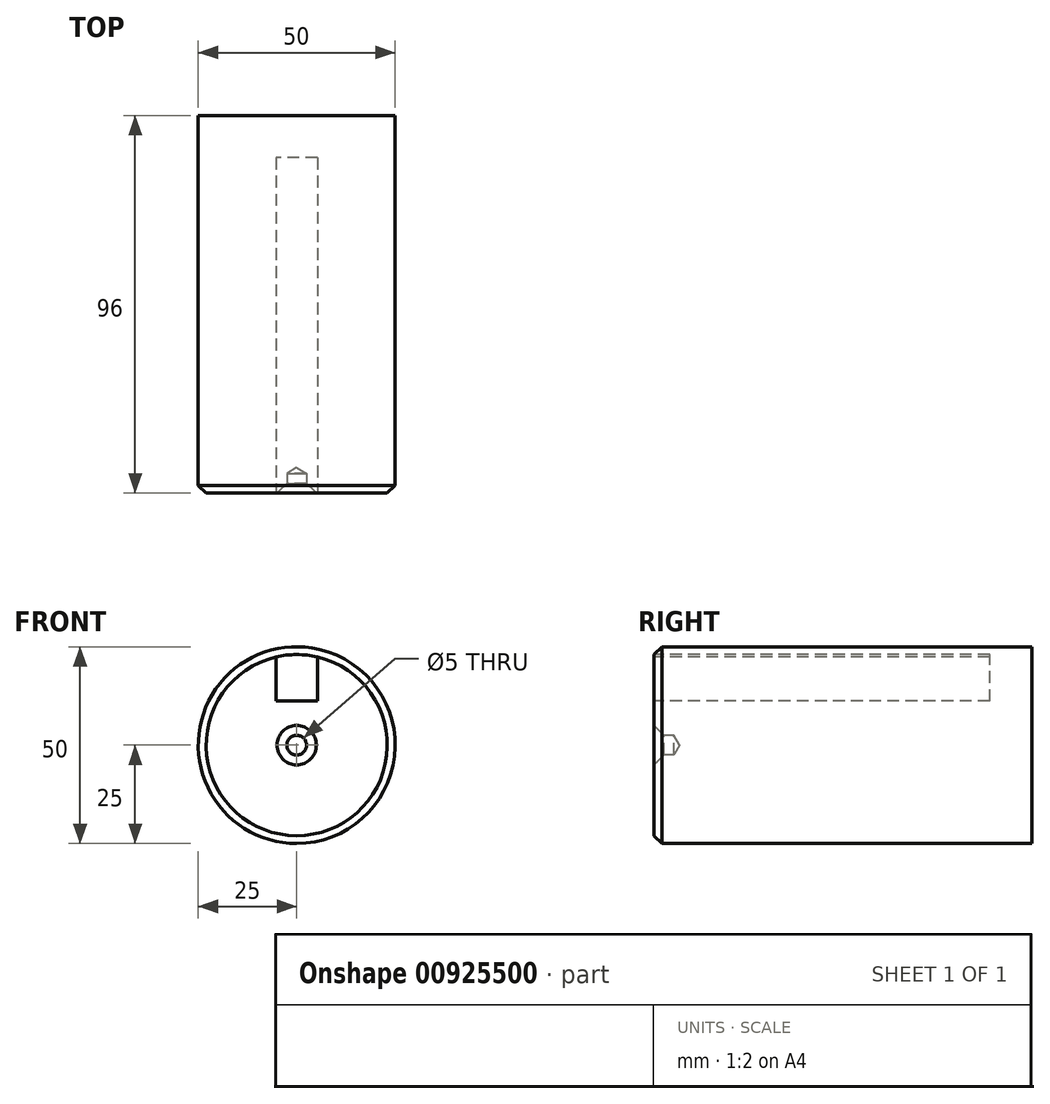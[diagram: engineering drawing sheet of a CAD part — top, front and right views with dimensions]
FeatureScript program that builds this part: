
annotation { "Feature Type Name" : "Feature", "Feature Type Description" : "" }
export const myFeature = defineFeature(function(context is Context, id is Id, definition is map)
    precondition{}
    {
        {
            var Q0;
            Q0=qCreatedBy(makeId("Front.planeOp"),FACE);
            var sketch = newSketch(context, id + "F0", { "sketchPlane" : qUnion([Q0])});
            skCircle(sketch, "E0", {"center": v(0, 0) * mm, "radius": 25 * mm});
            skSolve(sketch);
        }
        {
            var Q0;
            Q0=makeQuery(id+"F0.imprint","IMPRINT",FACE,{"disambiguationData":[TD([[makeQuery(id+"F0.imprint","IMPRINT",EDGE,{"derivedFrom":sQuery(id+"F0.wireOp",EDGE,"E0")}),1.0]])]});
            extrude(context, id + "F1", {"entities" : qUnion([Q0]), "depth" : 0 * mm, "offsetDistance" : 25 * mm, "hasSecondDirection" : true, "secondDirectionOppositeDirection" : true, "secondDirectionDepth" : 96 * mm});
        }
        {
            var Q0;
            Q0=makeQuery(id+"F1.opExtrude","CAP_EDGE",EDGE,{"disambiguationData":[OSD([sQuery(id+"F0.wireOp",EDGE,"E0")])],"isStart":false});
            chamfer(context, id + "F2", {"entities" : qUnion([Q0]), "chamferType" : ChamferType.OFFSET_ANGLE, "width" : 2 * mm, "oppositeDirection" : false, "angle" : 45 * degree, "tangentPropagation" : true});
        }
        {
            var Q0;
            Q0=makeQuery(id+"F1.opExtrude","CAP_FACE",FACE,{"disambiguationData":[OSD([sQuery(id+"F0.wireOp",EDGE,"E0")])],"isStart":false});
            var sketch = newSketch(context, id + "F3", { "sketchPlane" : qUnion([Q0])});
            skLineSegment(sketch, "E1", {"start": v(-5.25, 11.18) * mm, "end": v(4.75, 11.18) * mm});
            skLineSegment(sketch, "E2.MirrorCS", {"start": v(5.25, 11.18) * mm, "end": v(-4.75, 11.18) * mm});
            skLineSegment(sketch, "E3", {"start": v(5.25, 11.18) * mm, "end": v(5.25, 24.62) * mm});
            skLineSegment(sketch, "E4", {"start": v(-5.25, 11.18) * mm, "end": v(-5.25, 24.62) * mm});
            skArc(sketch, "E5", {"start": v(5.25, 24.62) * mm, "mid": v(0, 25.17) * mm, "end": v(-5.25, 24.62) * mm});
            skSolve(sketch);
        }
        {
            var Q0;
            {var subQ0=sQuery(id+"F3.wireOp",EDGE,"7XGwcHun-qUsb-BtbT-Hs0O-WZy7tM4iTs5j");Q0=makeQuery(id+"F3.imprint","IMPRINT",FACE,{"disambiguationData":[TD([[makeQuery(id+"F3.imprint","IMPRINT",EDGE,{"derivedFrom":subQ0}),1.0]])]});}
            var Q1;
            {var subQ6=sQuery(id+"F3.wireOp",EDGE,"E1");Q1=makeQuery(id+"F3.imprint","IMPRINT",FACE,{"disambiguationData":[TD([[makeQuery(id+"F3.imprint","IMPRINT",EDGE,{"derivedFrom":subQ6}),1.0]])]});}
            extrude(context, id + "F4", {"entities" : qUnion([Q0, Q1]), "operationType" : NewBodyOperationType.REMOVE, "oppositeDirection" : true, "depth" : 85.25 * mm, "offsetDistance" : 25 * mm});
        }
        {
            var Q0;
            Q0=qCreatedBy(makeId("Front.planeOp"),FACE);
            var sketch = newSketch(context, id + "F5", { "sketchPlane" : qUnion([Q0])});
            skPoint(sketch, "E6", {"position": v(0, 0) * mm});
            skSolve(sketch);
        }
        {
            var Q0;
            Q0=sQuery(id+"F5.wireOp",VERTEX,"E6");
            var Q1;
            Q1=makeQuery(id+"F1.opExtrude","SWEPT_BODY",BODY,{"disambiguationData":[OSD([sQuery(id+"F0.wireOp",EDGE,"E0")])]});
            hole(context, id + "F6", {"style" : HoleStyle.C_SINK, "endStyle" : HoleEndStyle.BLIND, "holeDiameter" : 5 * mm, "cSinkDiameter" : 10 * mm, "cSinkAngle" : 90 * degree, "majorDiameter" : 5 * mm, "holeDepth" : 5 * mm, "isTappedThrough" : true, "tappedDepth" : 12 * mm, "tapClearance" : 3, "locations" : qUnion([Q0]), "scope" : qUnion([Q1])});
        }
    });
